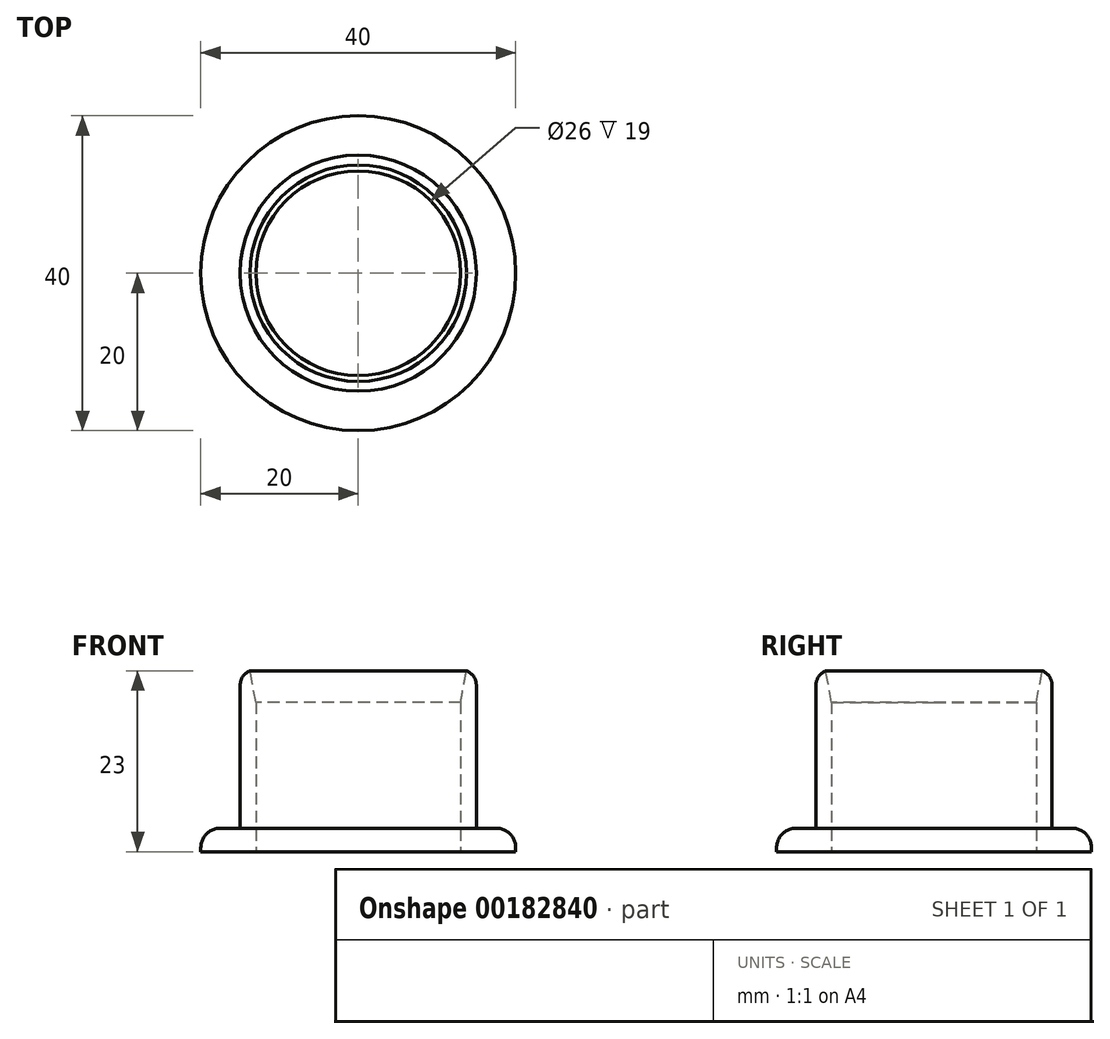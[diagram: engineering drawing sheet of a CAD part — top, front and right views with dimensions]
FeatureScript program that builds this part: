
annotation { "Feature Type Name" : "Feature", "Feature Type Description" : "" }
export const myFeature = defineFeature(function(context is Context, id is Id, definition is map)
    precondition{}
    {
        {
            var Q0;
            Q0=qCreatedBy(makeId("Top.planeOp"),FACE);
            var sketch = newSketch(context, id + "F0", { "sketchPlane" : qUnion([Q0])});
            skCircle(sketch, "E0", {"center": v(0, 0) * mm, "radius": 20 * mm});
            skCircle(sketch, "E1", {"center": v(0, 0) * mm, "radius": 13 * mm});
            skSolve(sketch);
        }
        {
            var Q0;
            Q0 = qSketchRegion(id + "F0", true);
            extrude(context, id + "F1", {"entities" : qUnion([Q0]), "depth" : 3 * mm});
        }
        {
            var Q0;
            Q0=makeQuery(id+"F1.opExtrude","CAP_FACE",FACE,{"disambiguationData":[OSD([sQuery(id+"F0.wireOp",EDGE,"E0"),sQuery(id+"F0.wireOp",EDGE,"E1")])],"isStart":false});
            var sketch = newSketch(context, id + "F2", { "sketchPlane" : qUnion([Q0])});
            skCircle(sketch, "E2.0", {"center": v(0, 0) * mm, "radius": 15 * mm});
            skCircle(sketch, "E3", {"center": v(0, 0) * mm, "radius": 13 * mm});
            skSolve(sketch);
        }
        {
            var Q0;
            Q0 = qSketchRegion(id + "F2", true);
            extrude(context, id + "F3", {"entities" : qUnion([Q0]), "operationType" : NewBodyOperationType.ADD, "depth" : 20 * mm});
        }
        {
            var Q0;
            Q0=makeQuery(id+"F1.opExtrude","CAP_EDGE",EDGE,{"disambiguationData":[OSD([sQuery(id+"F0.wireOp",EDGE,"E0")])],"isStart":false});
            fillet(context, id + "F4", {"entities" : qUnion([Q0]), "radius" : 2.5 * mm, "tangentPropagation" : true, "allowEdgeOverflow" : false});
        }
        {
            var Q0;
            Q0=makeQuery(id+"F3.opExtrude","CAP_EDGE",EDGE,{"disambiguationData":[OSD([sQuery(id+"F2.wireOp",EDGE,"E3")])],"isStart":false});
            chamfer(context, id + "F5", {"entities" : qUnion([Q0]), "chamferType" : ChamferType.TWO_OFFSETS, "width1" : .75 * mm, "oppositeDirection" : true, "width2" : 4 * mm, "tangentPropagation" : true});
        }
        {
            var Q0;
            Q0=makeQuery(id+"F3.opExtrude","CAP_EDGE",EDGE,{"disambiguationData":[OSD([sQuery(id+"F2.wireOp",EDGE,"E2.0")])],"isStart":false});
            fillet(context, id + "F6", {"entities" : qUnion([Q0]), "radius" : 2 * mm, "tangentPropagation" : true, "allowEdgeOverflow" : false});
        }
    });
